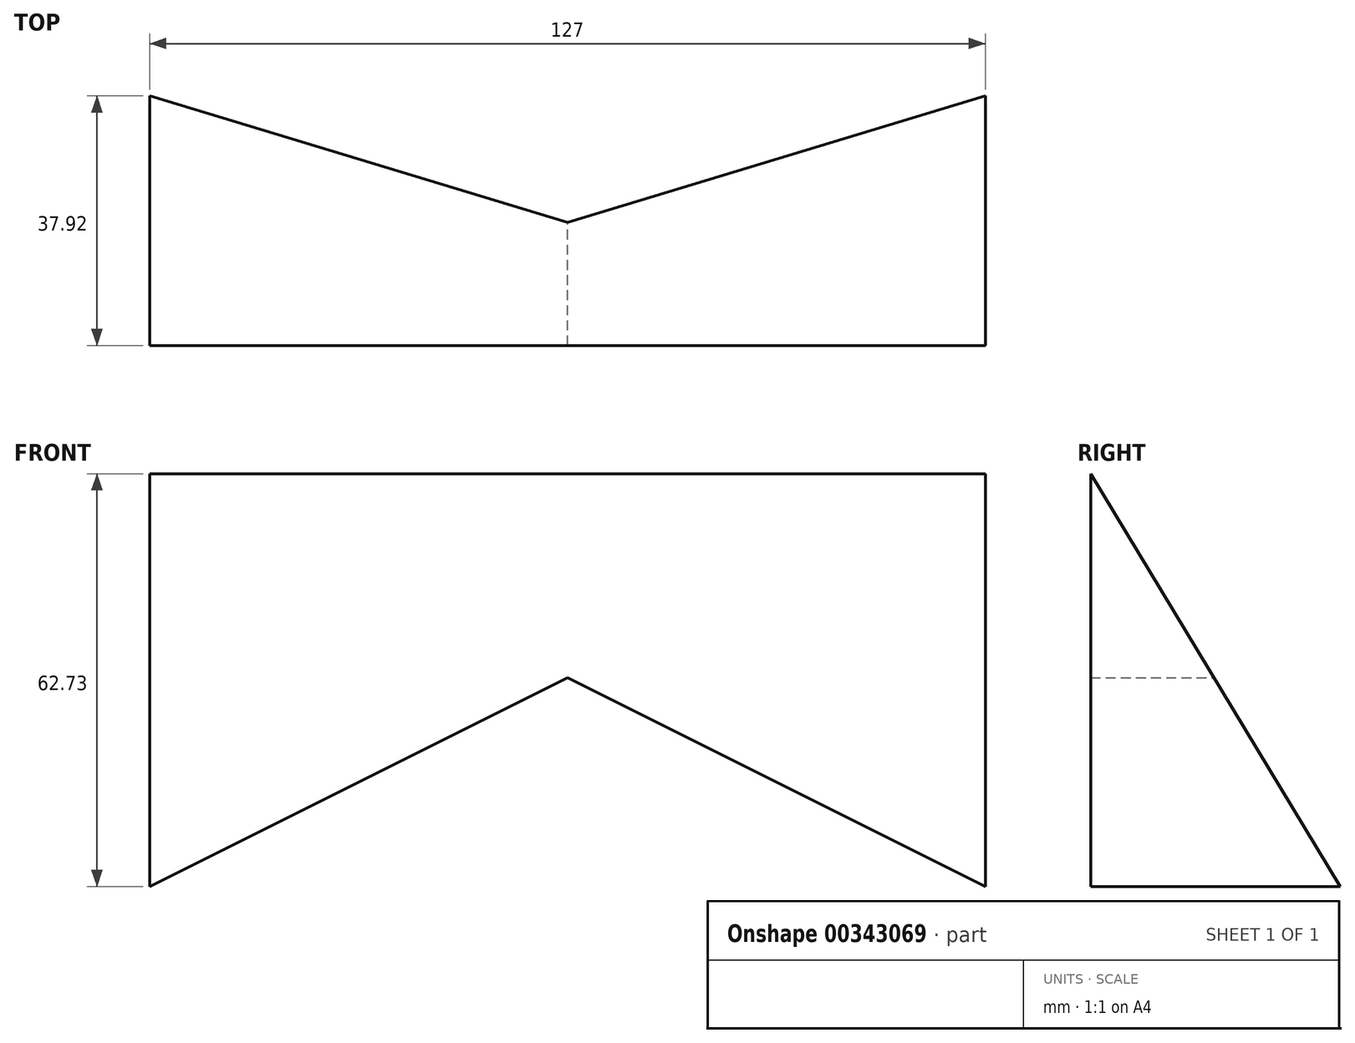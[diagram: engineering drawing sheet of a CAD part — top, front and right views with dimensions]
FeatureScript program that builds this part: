
annotation { "Feature Type Name" : "Feature", "Feature Type Description" : "" }
export const myFeature = defineFeature(function(context is Context, id is Id, definition is map)
    precondition{}
    {
        {
            var Q0;
            Q0=qCreatedBy(makeId("Front.planeOp"),FACE);
            var sketch = newSketch(context, id + "F0", { "sketchPlane" : qUnion([Q0])});
            skLineSegment(sketch, "E0", {"start": v(-63.5, 52.86) * mm, "end": v(0, 52.86) * mm});
            skLineSegment(sketch, "E1", {"start": v(0, 52.86) * mm, "end": v(63.5, 52.86) * mm});
            skLineSegment(sketch, "E2", {"start": v(-63.5, -10.64) * mm, "end": v(0, 21.11) * mm});
            skLineSegment(sketch, "E3", {"start": v(0, 21.11) * mm, "end": v(63.5, -10.64) * mm});
            skPoint(sketch, "E4.start.orphan", {"position": v(-63.5, 21.11) * mm});
            skPoint(sketch, "E5.start.orphan", {"position": v(63.5, 21.11) * mm});
            skLineSegment(sketch, "E6", {"start": v(-63.5, 52.86) * mm, "end": v(-63.5, -10.64) * mm});
            skLineSegment(sketch, "E7", {"start": v(63.5, 52.86) * mm, "end": v(63.5, -10.64) * mm});
            skSolve(sketch);
        }
        {
            var Q0;
            Q0 = qSketchRegion(id + "F0", true);
            extrude(context, id + "F1", {"entities" : qUnion([Q0]), "depth" : 38.1 * mm});
        }
        {
            var Q0;
            Q0=qCreatedBy(makeId("Right.planeOp"),FACE);
            var sketch = newSketch(context, id + "F2", { "sketchPlane" : qUnion([Q0])});
            skLineSegment(sketch, "E8", {"start": v(0, 53.2) * mm, "end": v(0, -10.93) * mm});
            skLineSegment(sketch, "E9", {"start": v(0, -10.93) * mm, "end": v(-38.77, 53.2) * mm});
            skLineSegment(sketch, "E10", {"start": v(-38.77, 53.2) * mm, "end": v(0, 53.2) * mm});
            skSolve(sketch);
        }
        {
            var Q0;
            Q0 = qSketchRegion(id + "F2", true);
            extrude(context, id + "F3", {"entities" : qUnion([Q0]), "operationType" : NewBodyOperationType.REMOVE, "oppositeDirection" : true, "depth" : 127 * mm, "hasSecondDirection" : true, "secondDirectionOppositeDirection" : false, "secondDirectionDepth" : 141.22 * mm});
        }
    });
